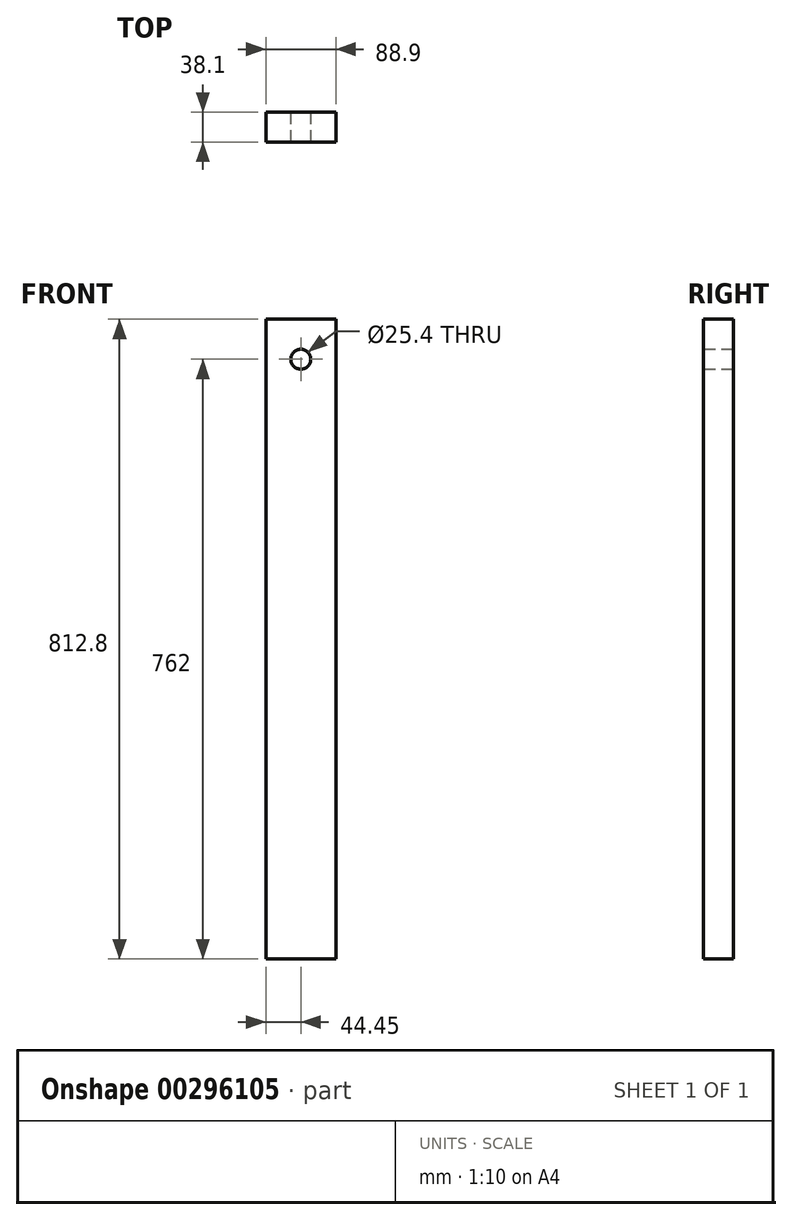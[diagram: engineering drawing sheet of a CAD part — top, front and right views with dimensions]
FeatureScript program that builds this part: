
annotation { "Feature Type Name" : "Feature", "Feature Type Description" : "" }
export const myFeature = defineFeature(function(context is Context, id is Id, definition is map)
    precondition{}
    {
        {
            var Q0;
            Q0=qCreatedBy(makeId("Front.planeOp"),FACE);
            var sketch = newSketch(context, id + "F0", { "sketchPlane" : qUnion([Q0])});
            skLineSegment(sketch, "E0.bottom", {"start": v(44.45, 406.4) * mm, "end": v(-44.45, 406.4) * mm});
            skLineSegment(sketch, "E0.top", {"start": v(44.45, -406.4) * mm, "end": v(-44.45, -406.4) * mm});
            skLineSegment(sketch, "E0.left", {"start": v(44.45, 406.4) * mm, "end": v(44.45, -406.4) * mm});
            skLineSegment(sketch, "E0.right", {"start": v(-44.45, 406.4) * mm, "end": v(-44.45, -406.4) * mm});
            skPoint(sketch, "E0.middle", {"position": v(0, 0) * mm});
            skPoint(sketch, "E1", {"position": v(0, 355.6) * mm});
            skPoint(sketch, "E2", {"position": v(-44.45, 355.6) * mm});
            skPoint(sketch, "E3", {"position": v(44.45, 355.6) * mm});
            skCircle(sketch, "E4", {"center": v(0, 355.6) * mm, "radius": 12.7 * mm});
            skSolve(sketch);
        }
        {
            var Q0;
            Q0=makeQuery(id+"F0.imprint","IMPRINT",FACE,{"disambiguationData":[TD([[makeQuery(id+"F0.imprint","IMPRINT",EDGE,{"derivedFrom":sQuery(id+"F0.wireOp",EDGE,"E0.bottom")}),1.0]])]});
            extrude(context, id + "F1", {"entities" : qUnion([Q0]), "depth" : 38.1 * mm});
        }
    });
